FCSTD DOCUMENT  (FreeCAD 0.21R33771 (Git))
Label: OJT1_T20R02_petagon
License: All rights reserved
LicenseURL: https://en.wikipedia.org/wiki/All_rights_reserved
objects: Sketcher::SketchObject×1, PartDesign::Body×1
note: 2 computed .brp shape members not serialized (recipe doc carries the construction recipe); baked Part::Feature solids carry a one-line shape summary decoded from their .brp

FEATURE [Sketcher::SketchObject] Sketch
  FullyConstrained = true
  MapMode = 5
  Support = -> [XY_Plane]
  sketch-geometry (7):
    g0: LineSegment StartX=-48.541 StartY=15.7719 StartZ=0 EndX=0 EndY=51.039 EndZ=0
    g1: LineSegment StartX=0 StartY=51.039 StartZ=0 EndX=48.541 EndY=15.7719 EndZ=0
    g2: LineSegment StartX=48.541 StartY=15.7719 StartZ=0 EndX=30 EndY=-41.2915 EndZ=0
    g3: LineSegment StartX=30 StartY=-41.2915 StartZ=0 EndX=-30 EndY=-41.2915 EndZ=0
    g4: LineSegment StartX=-30 StartY=-41.2915 StartZ=0 EndX=-48.541 EndY=15.7719 EndZ=0
    g5: LineSegment StartX=0 StartY=0 StartZ=0 EndX=-30 EndY=-41.2915 EndZ=0
    g6: LineSegment StartX=0 StartY=0 StartZ=0 EndX=-48.541 EndY=15.7719 EndZ=0
  constraints (17):
    c: Coincident(g0,g1)
    c: Coincident(g1,g2)
    c: Coincident(g2,g3)
    c: Coincident(g3,g4)
    c: Coincident(g4,g0)
    c: DistanceX(g3,g2) = 60
    c: PointOnObject(g0,g-2)
    c: Equal(g3,g4)
    c: Equal(g4,g0)
    c: Coincident(g5,g-1)
    c: Coincident(g5,g3)
    c: Coincident(g6,g5)
    c: Coincident(g6,g0)
    c: Angle(g-2,g6) = 1.25664
    c: Angle(g6,g5) = 1.25664
    c: Symmetric(g2,g3,g-2)
    c: Symmetric(g0,g1,g-2)
FEATURE [PartDesign::Body] Body
  Group = -> [Sketch]
  Origin = -> Origin
